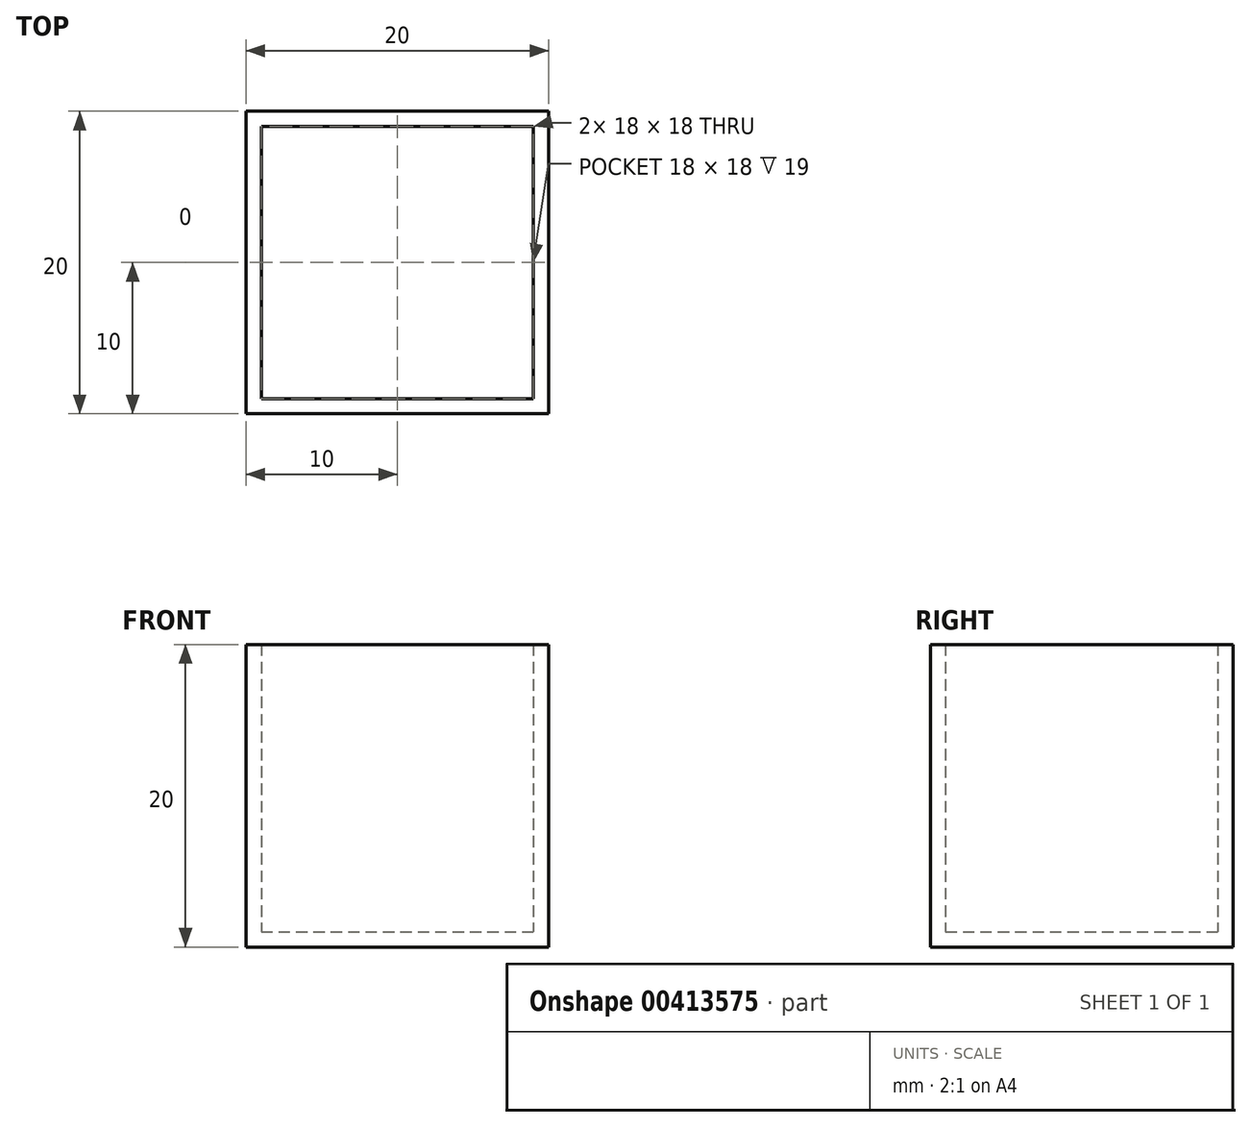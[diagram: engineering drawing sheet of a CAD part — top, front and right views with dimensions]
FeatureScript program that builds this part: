
annotation { "Feature Type Name" : "Feature", "Feature Type Description" : "" }
export const myFeature = defineFeature(function(context is Context, id is Id, definition is map)
    precondition{}
    {
        {
            var Q0;
            Q0=qCreatedBy(makeId("Top.planeOp"),FACE);
            var sketch = newSketch(context, id + "F0", { "sketchPlane" : qUnion([Q0])});
            skLineSegment(sketch, "E0.bottom", {"start": v(-10, -10) * mm, "end": v(10, -10) * mm});
            skLineSegment(sketch, "E0.top", {"start": v(-10, 10) * mm, "end": v(10, 10) * mm});
            skLineSegment(sketch, "E0.left", {"start": v(-10, -10) * mm, "end": v(-10, 10) * mm});
            skLineSegment(sketch, "E0.right", {"start": v(10, -10) * mm, "end": v(10, 10) * mm});
            skPoint(sketch, "E0.middle", {"position": v(0, 0) * mm});
            skSolve(sketch);
        }
        {
            var Q0;
            Q0 = qSketchRegion(id + "F0", true);
            var Q1;
            Q1=makeQuery(id+"F0.imprint","IMPRINT",FACE,{"disambiguationData":[TD([[makeQuery(id+"F0.imprint","IMPRINT",EDGE,{"derivedFrom":sQuery(id+"F0.wireOp",EDGE,"E0.bottom")}),1.0]])]});
            extrude(context, id + "F1", {"entities" : qUnion([Q0, Q1]), "depth" : 20 * mm});
        }
        {
            var Q0;
            Q0=makeQuery(id+"F1.opExtrude","CAP_FACE",FACE,{"disambiguationData":[OSD([sQuery(id+"F0.wireOp",EDGE,"E0.bottom"),sQuery(id+"F0.wireOp",EDGE,"E0.top"),sQuery(id+"F0.wireOp",EDGE,"E0.left"),sQuery(id+"F0.wireOp",EDGE,"E0.right")])],"isStart":false});
            var Q1;
            Q1=makeQuery(id+"F1.opExtrude","SWEPT_BODY",BODY,{"disambiguationData":[OSD([sQuery(id+"F0.wireOp",EDGE,"E0.bottom"),sQuery(id+"F0.wireOp",EDGE,"E0.top"),sQuery(id+"F0.wireOp",EDGE,"E0.left"),sQuery(id+"F0.wireOp",EDGE,"E0.right")])]});
            shell(context, id + "F2", {"entities" : qUnion([Q0]), "parts" : qUnion([Q1]), "thickness" : 1 * mm});
        }
    });
